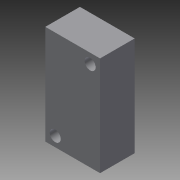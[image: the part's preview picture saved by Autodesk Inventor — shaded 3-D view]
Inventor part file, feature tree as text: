
AUTODESK INVENTOR PART (.ipt)
format: ipt  version: 2013 (Build 170138000, 138)  size: 76,288 bytes
history: native  units: in
note: dims shown in document units (in); Inventor stores cm internally (conversion verified against a paired STEP export)
features: extrude x1, sketch x1
ambient origin geometry x8: Origin, YZ Plane, XZ Plane, XY Plane, X Axis, Y Axis, Z Axis, Center Point
bodies: Solid1 (feature_tree)
feature tree (2):
  extrude  "Extrusion1"  Depth=0.623in
  sketch  "Sketch1"  dims[d0=1.131in d1=0.623in d2=0.125in d3=0.225in d4=0.125in d5=0.225in d6=0.394in d7=0.0in]
